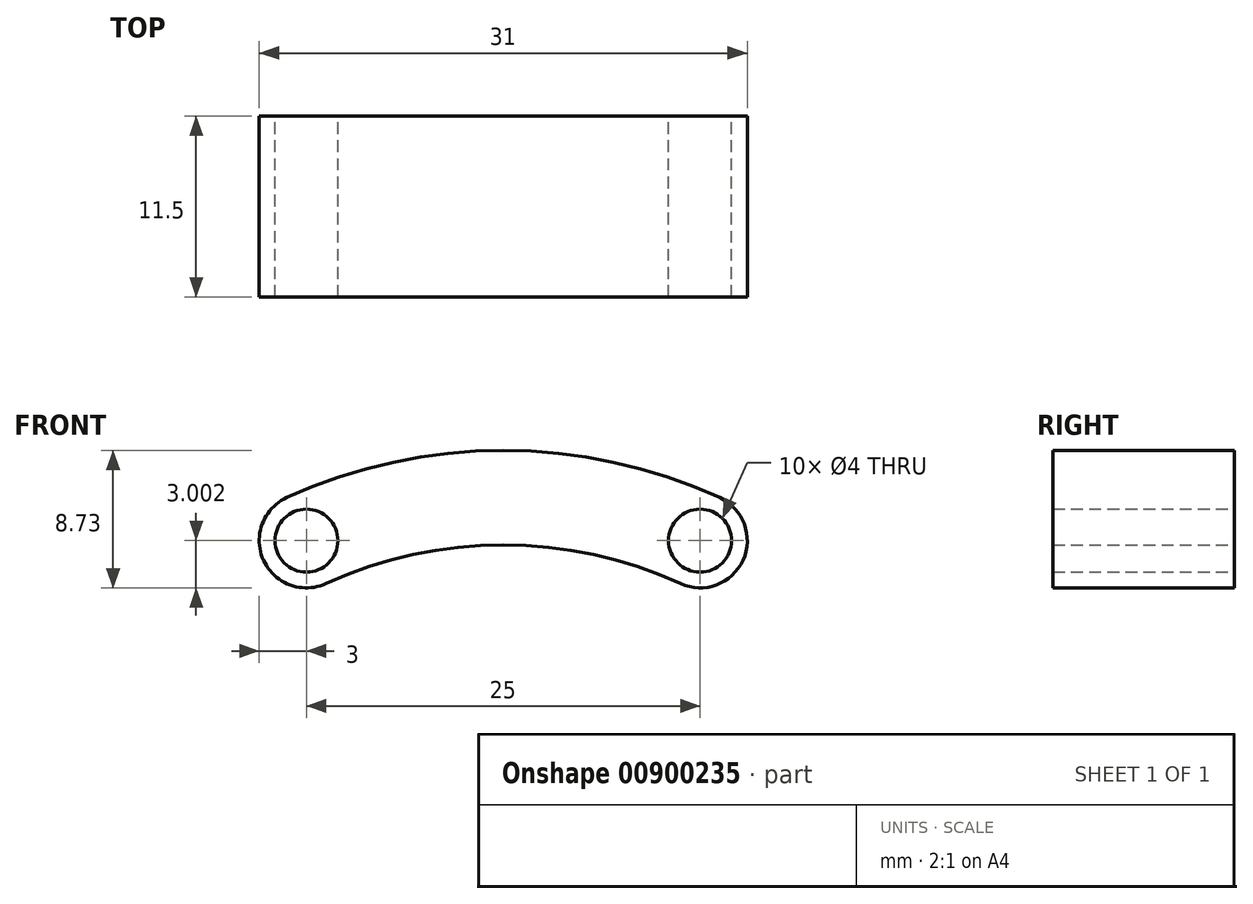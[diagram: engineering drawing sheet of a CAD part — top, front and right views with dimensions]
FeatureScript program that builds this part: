
annotation { "Feature Type Name" : "Feature", "Feature Type Description" : "" }
export const myFeature = defineFeature(function(context is Context, id is Id, definition is map)
    precondition{}
    {
        {
            var Q0;
            Q0=qCreatedBy(makeId("Front.planeOp"),FACE);
            var sketch = newSketch(context, id + "F0", { "sketchPlane" : qUnion([Q0])});
            skArc(sketch, "E0", {"start": v(13.75, 30) * mm, "mid": v(0, 33) * mm, "end": v(-13.75, 30) * mm});
            skArc(sketch, "E1.0", {"start": v(15.16, 25.89) * mm, "mid": v(0, 30) * mm, "end": v(-15.16, 25.89) * mm, "construction": true});
            skArc(sketch, "E2.0", {"start": v(11.25, 24.54) * mm, "mid": v(0, 27) * mm, "end": v(-11.25, 24.54) * mm});
            skArc(sketch, "E3", {"start": v(11.25, 24.54) * mm, "mid": v(15.23, 26.02) * mm, "end": v(13.75, 30) * mm});
            skArc(sketch, "E4", {"start": v(-13.75, 30) * mm, "mid": v(-15.23, 26.02) * mm, "end": v(-11.25, 24.54) * mm});
            skCircle(sketch, "E5", {"center": v(12.5, 27.27) * mm, "radius": 2 * mm});
            skCircle(sketch, "E6", {"center": v(-12.5, 27.27) * mm, "radius": 2 * mm});
            skLineSegment(sketch, "E7", {"start": v(0, 36.98) * mm, "end": v(0, 0) * mm, "construction": true});
            skSolve(sketch);
        }
        {
            var Q0;
            Q0 = qSketchRegion(id + "F0", true);
            extrude(context, id + "F1", {"entities" : qUnion([Q0]), "depth" : 11.5 * mm, "offsetDistance" : 25 * mm});
        }
    });
